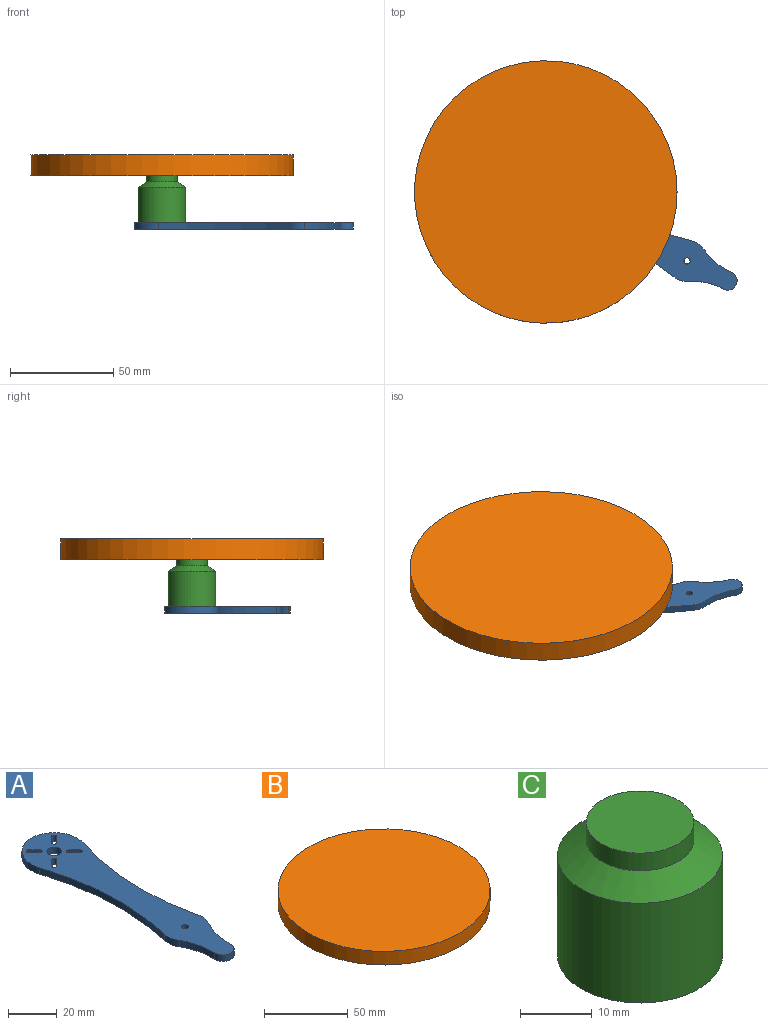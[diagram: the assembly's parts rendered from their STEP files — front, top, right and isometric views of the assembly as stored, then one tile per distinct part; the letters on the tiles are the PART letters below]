
ASSEMBLY  parts=3 mates=2
PART A: 28 faces, bbox 26.5x115.8x3.2 mm
  f0: cylinder r=1mm len=3.2mm, axis (0,0,-1), area 10.1mm2, adj f1,f19,f26,f27
  f1: plane 3.2x3.18mm, normal (0.71,0.71,0), area 14.4mm2, adj f0,f2,f26,f27
  f2: cylinder r=1mm len=3.2mm, axis (0,0,-1), area 10.1mm2, adj f1,f19,f26,f27
  f3: cylinder r=1mm len=3.2mm, axis (0,0,-1), area 10.1mm2, adj f4,f20,f26,f27
  f4: plane 3.2x3.18mm, normal (0.71,-0.71,0), area 14.4mm2, adj f3,f5,f26,f27
  f5: cylinder r=1mm len=3.2mm, axis (0,0,-1), area 10.1mm2, adj f4,f20,f26,f27
  f6: cylinder r=1mm len=3.2mm, axis (0,0,-1), area 10.1mm2, adj f7,f21,f26,f27
  f7: plane 3.2x3.18mm, normal (-0.71,-0.71,0), area 14.4mm2, adj f6,f8,f26,f27
  f8: cylinder r=1mm len=3.2mm, axis (0,0,-1), area 10.1mm2, adj f7,f21,f26,f27
  f9: cylinder r=1mm len=3.2mm, axis (0,0,-1), area 10.1mm2, adj f10,f22,f26,f27
  f10: plane 3.2x3.18mm, normal (-0.71,0.71,0), area 14.4mm2, adj f9,f11,f26,f27
  f11: cylinder r=1mm len=3.2mm, axis (0,0,-1), area 10.1mm2, adj f10,f22,f26,f27
  f12: cylinder r=125.74mm len=69.45mm, axis (0,0,-1), area 225.4mm2, adj f13,f24,f26,f27
  f13: cylinder r=10mm len=7.44mm, axis (0,0,-1), area 24.7mm2, adj f12,f14,f26,f27
  f14: cylinder r=30mm len=16.7mm, axis (0,0,-1), area 55.8mm2, adj f13,f15,f26,f27
  f15: cylinder r=4.5mm len=9mm, axis (0,0,-1), area 46.6mm2, adj f14,f16,f26,f27
  f16: cylinder r=30mm len=16.7mm, axis (0,0,-1), area 55.8mm2, adj f15,f17,f26,f27
  f17: cylinder r=10mm len=7.44mm, axis (0,0,-1), area 24.7mm2, adj f16,f18,f26,f27
  f18: cylinder r=125.74mm len=69.45mm, axis (0,0,-1), area 225.4mm2, adj f17,f24,f26,f27
  f19: plane 3.2x3.18mm, normal (-0.71,-0.71,0), area 14.4mm2, adj f0,f2,f26,f27
  f20: plane 3.2x3.18mm, normal (-0.71,0.71,0), area 14.4mm2, adj f3,f5,f26,f27
  f21: plane 3.2x3.18mm, normal (0.71,0.71,0), area 14.4mm2, adj f6,f8,f26,f27
  f22: plane 3.2x3.18mm, normal (0.71,-0.71,0), area 14.4mm2, adj f9,f11,f26,f27
  f23: cylinder r=3mm len=6mm, axis (0,0,-1), area 60.3mm2, adj f26,f27
  f24: cylinder r=13.25mm len=26.5mm, axis (0,0,-1), area 160.4mm2, adj f12,f18,f26,f27
  f25: cylinder r=1.5mm len=3.2mm, axis (0,0,-1), area 30.2mm2, adj f26,f27
  f26: plane 115.75x26.5mm, normal (0,0,1), area 1760.6mm2, adj f0,f1,f2,f3,f4,f5,f6,f7
  f27: plane 115.75x26.5mm, normal (0,0,-1), area 1760.6mm2, adj f0,f1,f2,f3,f4,f5,f6,f7
PART B: 3 faces, bbox 127x127x10 mm
  f0: cylinder r=63.5mm len=127mm, axis (0,0,-1), area 3989.8mm2, adj f1,f2
  f1: plane 127x127mm, normal (0,0,1), area 12667.7mm2, adj f0
  f2: plane 127x127mm, normal (0,0,-1), area 12667.7mm2, adj f0
PART C: 5 faces, bbox 23x23x22.7 mm
  f0: plane 23x23mm, normal (0,0,-1), area 415.5mm2, adj f1
  f1: cylinder r=11.5mm len=23mm, axis (0,0,1), area 1228.4mm2, adj f0,f2
  f2: cone r=11.5mm half-angle=55.7deg, axis (0,0,-1), area 288.9mm2, adj f1,f3
  f3: cylinder r=7.5mm len=15mm, axis (0,0,1), area 141.4mm2, adj f2,f4
  f4: plane 15x15mm, normal (0,0,1), area 176.7mm2, adj f3
PLACE A rot(axis=(0,0,1),64deg) t=(-2.07,-20.31,16.79)mm
PLACE B t=(17.74,-60.98,42.72)mm
PLACE C t=(-33.43,13,19.99)mm
MATE revolute B.f0 <-> C.f1  axis (0,0,-1) through (-70.38,13,42.72)mm
MATE revolute C.f1 <-> A.f23  axis (0,0,-1) through (-70.38,13,19.99)mm
